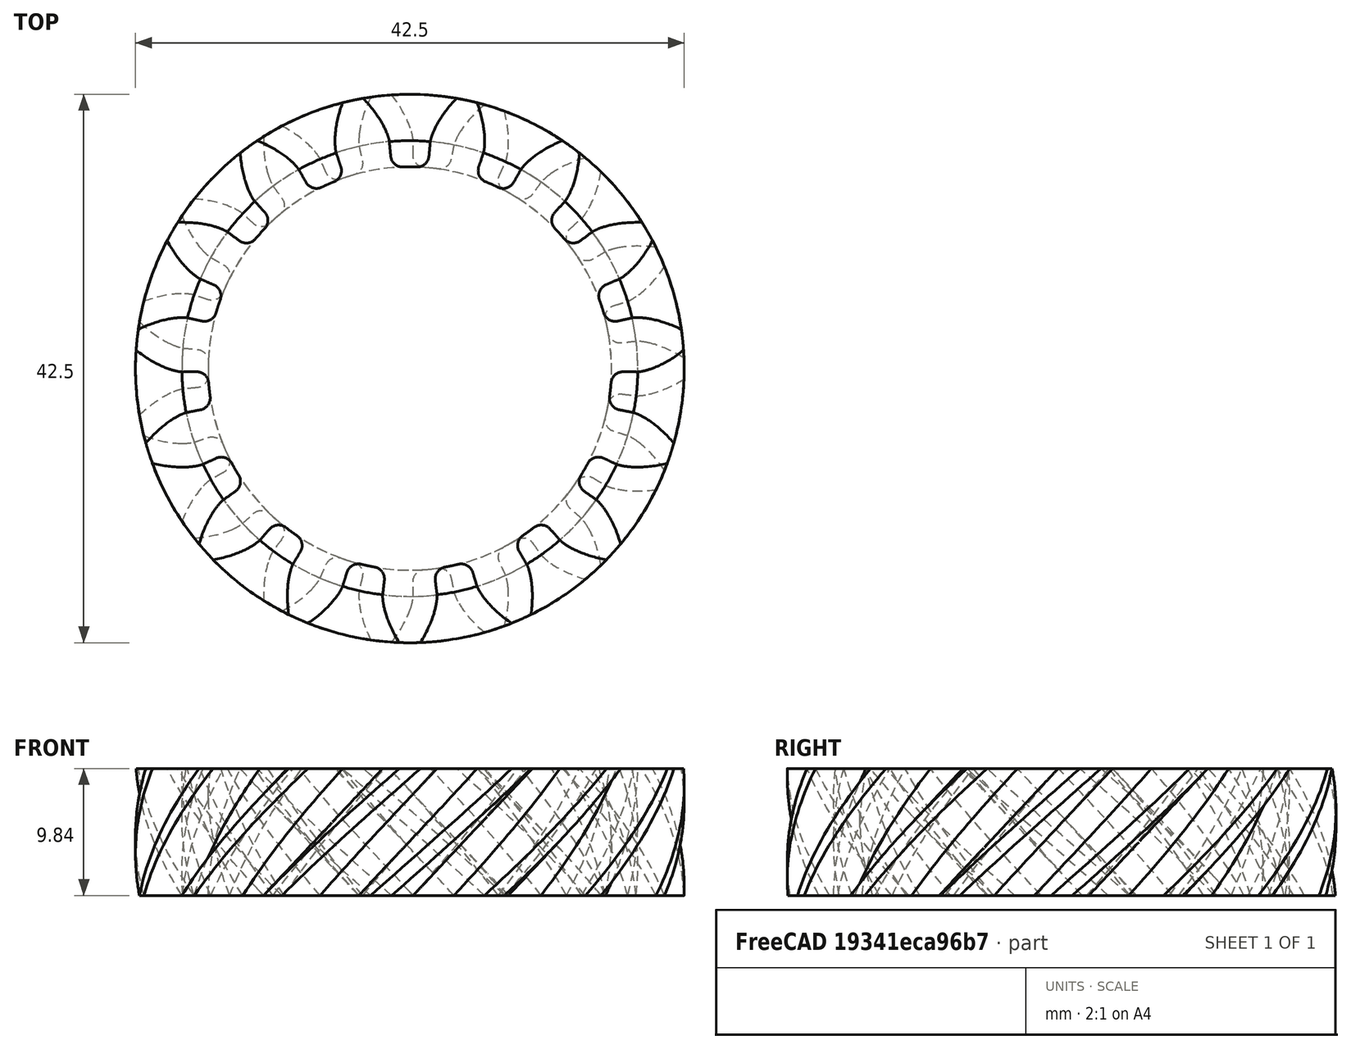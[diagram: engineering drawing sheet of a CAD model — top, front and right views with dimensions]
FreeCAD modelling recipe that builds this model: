
FCSTD DOCUMENT  (FreeCAD 0.20R29177 +426 (Git))
Label: Engranaje oblicuo
License: All rights reserved
LicenseURL: http://en.wikipedia.org/wiki/All_rights_reserved
objects: Part::Part2DObjectPython×7, Part::Loft×1
note: 8 computed .brp shape members not serialized (recipe doc carries the construction recipe); baked Part::Feature solids carry a one-line shape summary decoded from their .brp

FEATURE [Part::Part2DObjectPython] InvoluteGear  # Draft 2D object (typed FeaturePython)
  ExternalGear = true
  HighPrecision = true
  Modules = 2.5
  NumberOfTeeth = 15
  PressureAngle = 20
FEATURE [Part::Part2DObjectPython] InvoluteGear001  # Draft 2D object (typed FeaturePython)
  ExternalGear = true
  HighPrecision = true
  Modules = 2.5
  NumberOfTeeth = 15
  Placement = pos=(0,0,1.64) rot=(0,0,1;0.087266rad)
  PressureAngle = 20
FEATURE [Part::Part2DObjectPython] InvoluteGear002  # Draft 2D object (typed FeaturePython)
  ExternalGear = true
  HighPrecision = true
  Modules = 2.5
  NumberOfTeeth = 15
  Placement = pos=(0,0,3.28) rot=(0,0,1;0.174533rad)
  PressureAngle = 20
FEATURE [Part::Part2DObjectPython] InvoluteGear003  # Draft 2D object (typed FeaturePython)
  ExternalGear = true
  HighPrecision = true
  Modules = 2.5
  NumberOfTeeth = 15
  Placement = pos=(0,0,4.92) rot=(0,0,1;0.261799rad)
  PressureAngle = 20
FEATURE [Part::Part2DObjectPython] InvoluteGear004  # Draft 2D object (typed FeaturePython)
  ExternalGear = true
  HighPrecision = true
  Modules = 2.5
  NumberOfTeeth = 15
  Placement = pos=(0,0,6.56) rot=(0,0,1;0.349066rad)
  PressureAngle = 20
FEATURE [Part::Part2DObjectPython] InvoluteGear005  # Draft 2D object (typed FeaturePython)
  ExternalGear = true
  HighPrecision = true
  Modules = 2.5
  NumberOfTeeth = 15
  Placement = pos=(0,0,8.2) rot=(0,0,1;0.436332rad)
  PressureAngle = 20
FEATURE [Part::Part2DObjectPython] InvoluteGear006  # Draft 2D object (typed FeaturePython)
  ExternalGear = true
  HighPrecision = true
  Modules = 2.5
  NumberOfTeeth = 15
  Placement = pos=(0,0,9.84) rot=(0,0,1;0.523599rad)
  PressureAngle = 20
FEATURE [Part::Loft] Loft
  Closed = false
  MaxDegree = 5
  Ruled = false
  Sections = -> [InvoluteGear,InvoluteGear001,InvoluteGear002,InvoluteGear003,InvoluteGear004,InvoluteGear005,InvoluteGear006]
  Solid = true
